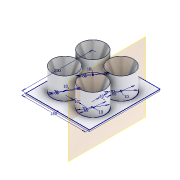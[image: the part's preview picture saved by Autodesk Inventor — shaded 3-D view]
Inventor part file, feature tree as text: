
AUTODESK INVENTOR PART (.ipt)
format: ipt  version: 2020.3 (Build 243373010, 373A)  size: 162,816 bytes
history: native  units: mm
features: sketch x2, plane x1, revolve x1, pattern_linear x1, extrude x1
ambient origin geometry x8: Origin, YZ Plane, XZ Plane, XY Plane, X Axis, Y Axis, Z Axis, Center Point
bodies: Solid1 (feature_tree)
feature tree (6):
  sketch  "Sketch1"  dims[d0=180.0mm d1=200.0mm]
  plane  "Work Plane1"
  revolve  "Revolution1"  [1 undecoded]
  pattern_linear  "Rectangular Pattern1"  Spacing1=10.0mm  [1 undecoded]
  extrude  "Extrusion1"  Depth=10.0mm
  sketch  "Sketch2"  dims[d2=70.0mm d3=70.0mm d4=70.0mm d5=70.0mm d6=10.0mm d7=10.0mm d8=68.0mm d9=68.0mm d10=68.0mm d11=68.0mm d12=10.0mm d13=10.0mm d14=10.0mm d15=10.0mm d16=-50.0mm d17=60.0mm d18=0.0mm d20=90.0deg d21=20.0mm d23=-80.0mm d24=20.0mm d26=80.0mm d27=5.0mm d28=0.0mm]
note: 2 required parameter values undecoded (feature->parameter linkage not recoverable at this tier; creation-order binding heuristic only, values carry confidence <= 0.55)